# Revit family: CONV_Pholc_GnrlPrpseLmnrs_ApolloPendant59
name_source: partatom
category: Lighting Fixtures
revit_build: Autodesk Revit Architecture 2015 (Build: 20140322_1515(x64)
units: mm (PartAtom-declared; Revit-internal decimal feet)

## types (2) — shared parameters
AssetType = Fixed
BIMObjectName = CONV_Pholc_GnrlPrpseLmnrs_ApolloPendant59
Brand = Pholc
CableLength = 300 mm  [stored 0.984252 ft]
Category = Pendant
Collection = Apollo
Color Filter = 16777215
ConvergoRefNr = 0103-1801-0002-SE
Designer = Broberg & Ridderstrale
Dimming = None
Dimming Lamp Color Temperature Shift = <None>
DurationUnit = Year
Emit Shape Visible in Rendering = No
Emit from Circle Diameter = 158 mm
ExpiringDate = 07/2018
Features = Ceiling plug
Finish = Polished aluminum/brass
HasProtectiveEarth = No
IfcExportAs = IfcLightFixtureType
IfcExportType = NOTDEFINED
Light Source Symbol Length = 3048 mm  [stored 10 ft]
LightFixtureMountingType = Suspended
LightFixturePlacingType = Ceiling
LightFixtureTertiaryMaterial = Textile Black
Manufacturer = Pholc
ManufacturerName = Pholc
ManufacturerURL = https://www.pholc.se
Material = Aluminum, brass
ModelHeight = 590 mm
NBSDescription = General purpose luminaires
NBSReference = 90-60-50/405
Name = GnrlPrpseLmnrs_ApolloPendant59
NominalCurrent = 0 A
NominalDiameter = 125 mm  [stored 0.410105 ft]
NominalFrequencyRange = 50 Hz
NominalHeight = 743 mm
NominalLength = 125 mm  [stored 0.410105 ft]
NominalRadius = 63 mm
NominalVoltage = 230 V
NominalVoltageCalc = 0 V
NominalWidth = 125 mm  [stored 0.410105 ft]
NumberOfPoles = 1
PhaseAngle = 0.00°
ProductInformation = Apollo is a lamp with a very high sense of material presence.
The assembly of conical shapes that balances on top of each other like spinning gyros, emphasizes the downward force in a pendant lamp and create both a dynamic and static expression.
Machine-turned from a solid piece of brass or aluminum, these shapes show not just a beautiful raw metal surface but also alludes to its mass and weight.
The lamp comes in three different heights and a variation of colors enabling a multitude of hanging combinations as groups or in singles.
Apollo is ideal to hang over a table or a counter, in a composed cluster or an outstretched row, letting the choice of material and color complete or match the surrounding setting.
Shape = Sculptured
Size = 125x125x743 mm
Spot Beam Angle = 30.00°
Spot Field Angle = 90.00°
Tilt Angle = 90.00°
TotalWattage = 20 W
URL = https://www.pholc.se
Uniclass2 = Pr_70_70_49_86
Uniclass2015Description = Suspended luminaires
Uniclass2015Reference = Pr_70_70_48_86
UsageCurrent = 0 A
Version = 1
VersionDate = 12/02/2018
WarrantyDurationUnit = Year
zero-valued in all types: DefaultElevation, ElectricalDeviceNominalPower, MaintenanceFactor, NumberOfSources

## per-type parameters (varying)
| type | ArticleNumber | Color | LightFixtureMainMaterial | LightFixtureSecondaryMaterial | Model | ModelNumber |
| Apollo 59 Deep sea/brass | 592117 | Deep Sea | Brass | Deep Sea | Apollo 59 Pendant Deep  Sea, Polished Brass | 592117 |
| Apollo 59 Light grey/aluminum | 592119 | Light Grey | Aluminum | Light Grey | Apollo 59 Pendant Light Grey, Polished Aluminum | 592119 |

note: [stored X ft] marks values corroborated as IEEE doubles in the binary element streams (Revit-internal decimal feet)

## geometry (parser evidence)
native form markers: Sweep x6
no freeform markers — native parametric forms only
